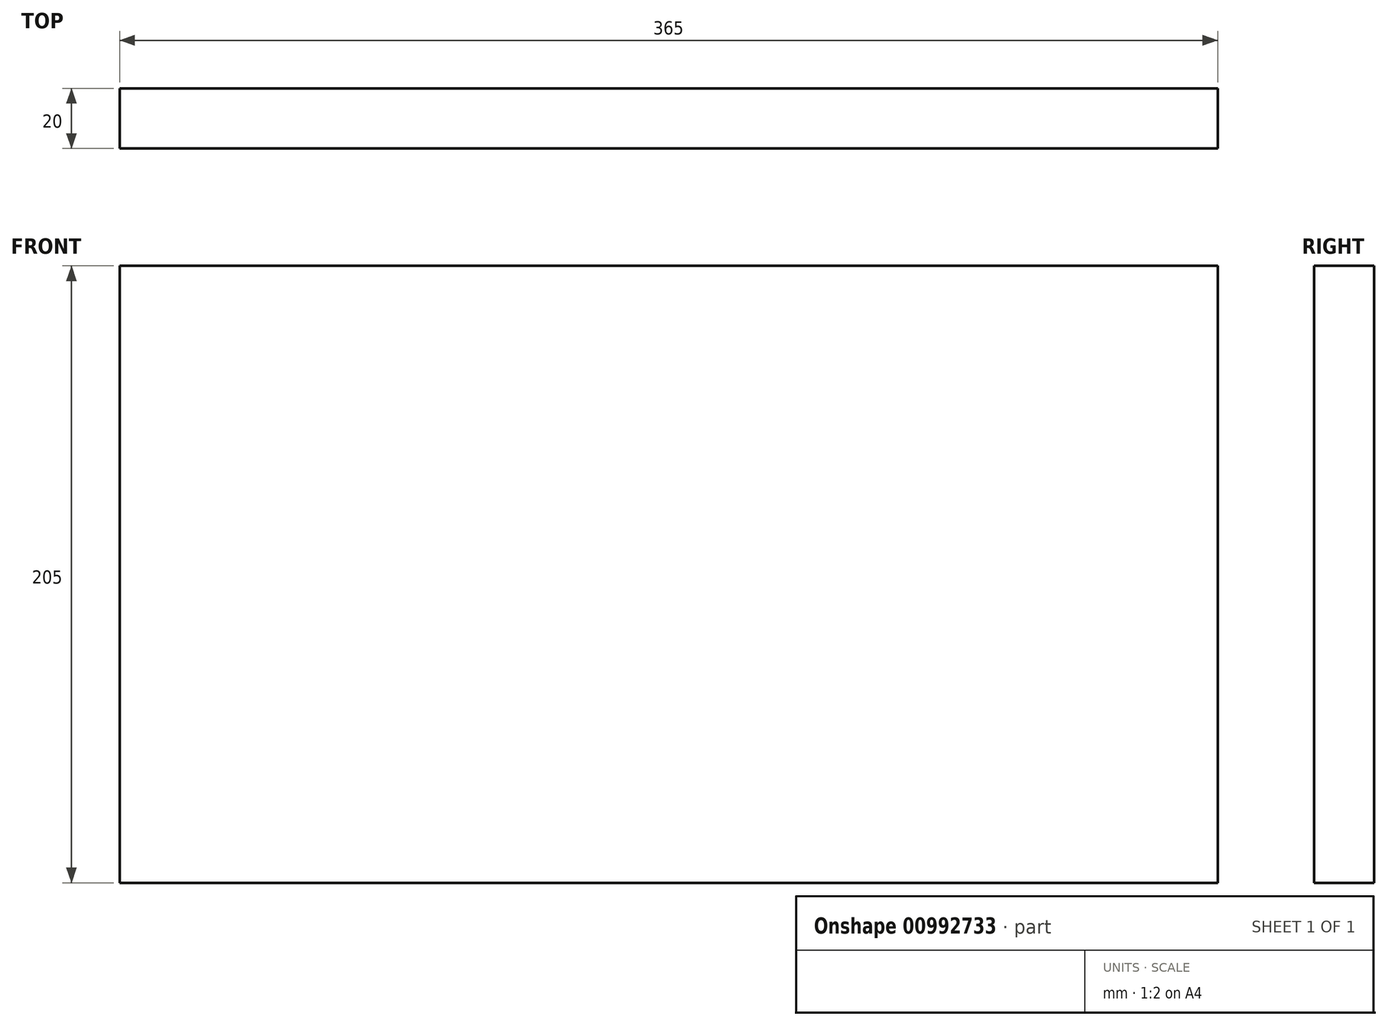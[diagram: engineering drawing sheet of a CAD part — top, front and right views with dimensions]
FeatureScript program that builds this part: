
annotation { "Feature Type Name" : "Feature", "Feature Type Description" : "" }
export const myFeature = defineFeature(function(context is Context, id is Id, definition is map)
    precondition{}
    {
        {
            var Q0;
            Q0=qCreatedBy(makeId("Top.planeOp"),FACE);
            var sketch = newSketch(context, id + "F0", { "sketchPlane" : qUnion([Q0])});
            skLineSegment(sketch, "E0.bottom", {"start": v(182.5, 265) * mm, "end": v(-182.5, 265) * mm});
            skLineSegment(sketch, "E0.top", {"start": v(182.5, -265) * mm, "end": v(-182.5, -265) * mm});
            skLineSegment(sketch, "E0.left", {"start": v(182.5, 265) * mm, "end": v(182.5, -265) * mm});
            skLineSegment(sketch, "E0.right", {"start": v(-182.5, 265) * mm, "end": v(-182.5, -265) * mm});
            skPoint(sketch, "E0.middle", {"position": v(0, 0) * mm});
            skSolve(sketch);
        }
        {
            var Q0;
            Q0=makeQuery(id+"F0.imprint","IMPRINT",FACE,{"disambiguationData":[TD([[makeQuery(id+"F0.imprint","IMPRINT",EDGE,{"derivedFrom":sQuery(id+"F0.wireOp",EDGE,"E0.bottom")}),1.0]])]});
            extrude(context, id + "F1", {"entities" : qUnion([Q0]), "depth" : 10 * mm, "offsetDistance" : 25 * mm});
        }
        {
            var Q0;
            Q0=makeQuery(id+"F1.opExtrude","CAP_FACE",FACE,{"disambiguationData":[OSD([sQuery(id+"F0.wireOp",EDGE,"E0.bottom"),sQuery(id+"F0.wireOp",EDGE,"E0.top"),sQuery(id+"F0.wireOp",EDGE,"E0.left"),sQuery(id+"F0.wireOp",EDGE,"E0.right")])],"isStart":false});
            var sketch = newSketch(context, id + "F2", { "sketchPlane" : qUnion([Q0])});
            skLineSegment(sketch, "E1.bottom", {"start": v(-182.5, 265) * mm, "end": v(-162.5, 265) * mm});
            skLineSegment(sketch, "E1.top", {"start": v(-182.5, -265) * mm, "end": v(-162.5, -265) * mm});
            skLineSegment(sketch, "E1.left", {"start": v(-182.5, 265) * mm, "end": v(-182.5, -265) * mm});
            skLineSegment(sketch, "E1.right", {"start": v(-162.5, 265) * mm, "end": v(-162.5, -265) * mm});
            skLineSegment(sketch, "E2.bottom", {"start": v(182.5, 265) * mm, "end": v(162.5, 265) * mm});
            skLineSegment(sketch, "E2.top", {"start": v(182.5, -265) * mm, "end": v(162.5, -265) * mm});
            skLineSegment(sketch, "E2.left", {"start": v(182.5, 265) * mm, "end": v(182.5, -265) * mm});
            skLineSegment(sketch, "E2.right", {"start": v(162.5, 265) * mm, "end": v(162.5, -265) * mm});
            skLineSegment(sketch, "E3.bottom", {"start": v(-162.5, -265) * mm, "end": v(162.5, -265) * mm});
            skLineSegment(sketch, "E3.top", {"start": v(-162.5, -245) * mm, "end": v(162.5, -245) * mm});
            skLineSegment(sketch, "E3.left", {"start": v(-162.5, -265) * mm, "end": v(-162.5, -245) * mm});
            skLineSegment(sketch, "E3.right", {"start": v(162.5, -265) * mm, "end": v(162.5, -245) * mm});
            skLineSegment(sketch, "E4.bottom", {"start": v(162.5, 265) * mm, "end": v(-162.5, 265) * mm});
            skLineSegment(sketch, "E4.top", {"start": v(162.5, 245) * mm, "end": v(-162.5, 245) * mm});
            skLineSegment(sketch, "E4.left", {"start": v(162.5, 265) * mm, "end": v(162.5, 245) * mm});
            skLineSegment(sketch, "E4.right", {"start": v(-162.5, 265) * mm, "end": v(-162.5, 245) * mm});
            skSolve(sketch);
        }
        {
            var Q0;
            Q0=makeQuery(id+"F2.imprint","IMPRINT",FACE,{"disambiguationData":[TD([[makeQuery(id+"F2.imprint","IMPRINT",EDGE,{"derivedFrom":sQuery(id+"F2.wireOp",EDGE,"E1.bottom")}),1.0]])]});
            var Q1;
            Q1=makeQuery(id+"F2.imprint","IMPRINT",FACE,{"disambiguationData":[TD([[makeQuery(id+"F2.imprint","IMPRINT",EDGE,{"derivedFrom":sQuery(id+"F2.wireOp",EDGE,"E4.bottom")}),1.0]])]});
            var Q2;
            Q2=makeQuery(id+"F2.imprint","IMPRINT",FACE,{"disambiguationData":[TD([[makeQuery(id+"F2.imprint","IMPRINT",EDGE,{"derivedFrom":sQuery(id+"F2.wireOp",EDGE,"E2.bottom")}),1.0]])]});
            var Q3;
            Q3=makeQuery(id+"F2.imprint","IMPRINT",FACE,{"disambiguationData":[TD([[makeQuery(id+"F2.imprint","IMPRINT",EDGE,{"derivedFrom":sQuery(id+"F2.wireOp",EDGE,"E3.bottom")}),-1.0]])]});
            extrude(context, id + "F3", {"entities" : qUnion([Q0, Q1, Q2, Q3]), "operationType" : NewBodyOperationType.ADD, "depth" : 195 * mm, "offsetDistance" : 25 * mm});
        }
        {
            var Q0;
            Q0=makeQuery(id+"F3.opExtrude","CAP_FACE",FACE,{"disambiguationData":[OSD([sQuery(id+"F2.wireOp",EDGE,"E1.bottom"),sQuery(id+"F2.wireOp",EDGE,"E1.top"),sQuery(id+"F2.wireOp",EDGE,"E1.left"),sQuery(id+"F2.wireOp",EDGE,"E1.right"),sQuery(id+"F2.wireOp",EDGE,"E2.bottom"),sQuery(id+"F2.wireOp",EDGE,"E2.top"),sQuery(id+"F2.wireOp",EDGE,"E2.left"),sQuery(id+"F2.wireOp",EDGE,"E2.right"),sQuery(id+"F2.wireOp",EDGE,"E3.bottom"),sQuery(id+"F2.wireOp",EDGE,"E3.top"),sQuery(id+"F2.wireOp",EDGE,"E4.bottom"),sQuery(id+"F2.wireOp",EDGE,"E4.top")])],"isStart":false});
            var sketch = newSketch(context, id + "F4", { "sketchPlane" : qUnion([Q0])});
            skLineSegment(sketch, "E5.bottom", {"start": v(-182.5, 265) * mm, "end": v(182.5, 265) * mm});
            skLineSegment(sketch, "E5.top", {"start": v(-182.5, -245) * mm, "end": v(182.5, -245) * mm});
            skLineSegment(sketch, "E5.left", {"start": v(-182.5, 265) * mm, "end": v(-182.5, -245) * mm});
            skLineSegment(sketch, "E5.right", {"start": v(182.5, 265) * mm, "end": v(182.5, -245) * mm});
            skSolve(sketch);
        }
        {
            var Q0;
            Q0=makeQuery(id+"F4.imprint","IMPRINT",FACE,{"disambiguationData":[TD([[makeQuery(id+"F4.imprint","IMPRINT",EDGE,{"derivedFrom":sQuery(id+"F4.wireOp",EDGE,"E5.bottom")}),1.0]])]});
            var Q1;
            {var subQ1=makeQuery(id+"F3.opExtrude","CAP_EDGE",EDGE,{"disambiguationData":[OSD([sQuery(id+"F2.wireOp",EDGE,"E1.right")])],"isStart":false});Q1=makeQuery(id+"F4.imprint","IMPRINT",FACE,{"disambiguationData":[TD([[makeQuery(id+"F4.imprint","IMPRINT",EDGE,{"derivedFrom":subQ1}),1.0]])]});}
            extrude(context, id + "F5", {"entities" : qUnion([Q0, Q1]), "operationType" : NewBodyOperationType.REMOVE, "endBound" : BoundingType.THROUGH_ALL, "oppositeDirection" : true, "depth" : 25 * mm, "offsetDistance" : 25 * mm});
        }
    });
